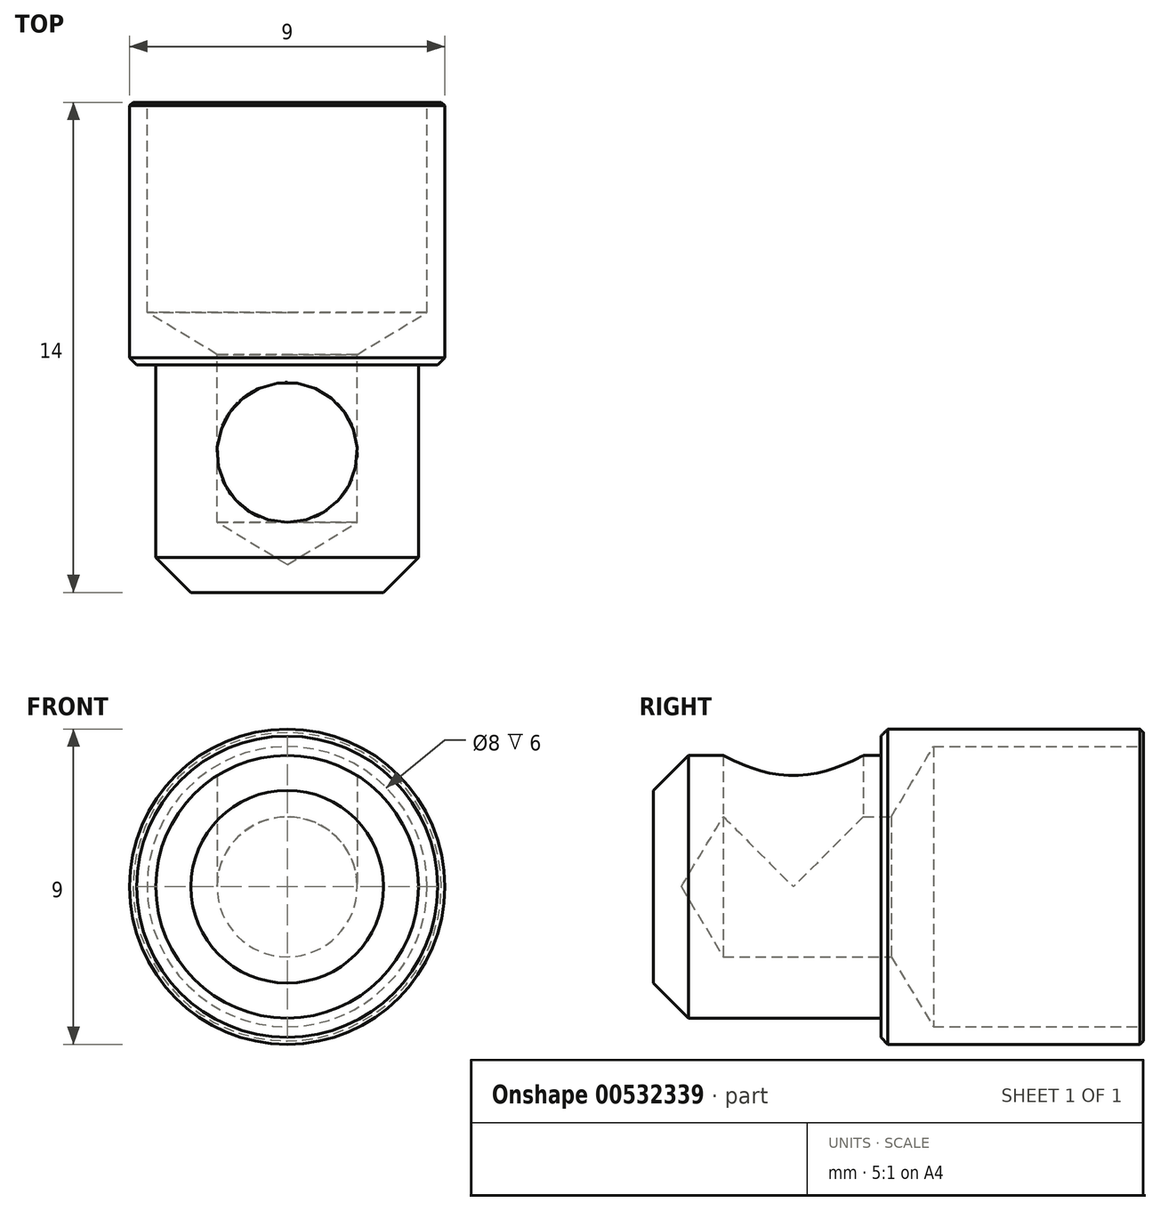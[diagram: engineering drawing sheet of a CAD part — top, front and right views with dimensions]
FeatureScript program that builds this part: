
annotation { "Feature Type Name" : "Feature", "Feature Type Description" : "" }
export const myFeature = defineFeature(function(context is Context, id is Id, definition is map)
    precondition{}
    {
        {
            var Q0;
            Q0=qCreatedBy(makeId("Front.planeOp"),FACE);
            var sketch = newSketch(context, id + "F0", { "sketchPlane" : qUnion([Q0])});
            skCircle(sketch, "E0", {"center": v(0, 0) * mm, "radius": 3.75 * mm});
            skSolve(sketch);
        }
        {
            var Q0;
            Q0 = qSketchRegion(id + "F0", true);
            extrude(context, id + "F1", {"entities" : qUnion([Q0]), "depth" : 6.5 * mm, "offsetDistance" : 25 * mm});
        }
        {
            var Q0;
            Q0=makeQuery(id+"F1.opExtrude","CAP_EDGE",EDGE,{"disambiguationData":[OSD([sQuery(id+"F0.wireOp",EDGE,"E0")])],"isStart":false});
            chamfer(context, id + "F2", {"entities" : qUnion([Q0]), "width" : 1 * mm, "tangentPropagation" : true});
        }
        {
            var Q0;
            Q0=makeQuery(id+"F1.opExtrude","CAP_FACE",FACE,{"disambiguationData":[OSD([sQuery(id+"F0.wireOp",EDGE,"E0")])],"isStart":true});
            var sketch = newSketch(context, id + "F3", { "sketchPlane" : qUnion([Q0])});
            skCircle(sketch, "E1", {"center": v(0, 0) * mm, "radius": 4.5 * mm});
            skSolve(sketch);
        }
        {
            var Q0;
            Q0 = qSketchRegion(id + "F3", true);
            extrude(context, id + "F4", {"entities" : qUnion([Q0]), "operationType" : NewBodyOperationType.ADD, "depth" : 7.5 * mm, "offsetDistance" : 25 * mm});
        }
        {
            var Q0;
            Q0=makeQuery(id+"F4.opExtrude","CAP_EDGE",EDGE,{"disambiguationData":[OSD([sQuery(id+"F3.wireOp",EDGE,"E1")])],"isStart":true});
            chamfer(context, id + "F5", {"entities" : qUnion([Q0]), "width" : 0.2 * mm, "tangentPropagation" : true});
        }
        {
            var Q0;
            Q0=makeQuery(id+"F4.opExtrude","CAP_FACE",FACE,{"disambiguationData":[OSD([sQuery(id+"F3.wireOp",EDGE,"E1")])],"isStart":false});
            var sketch = newSketch(context, id + "F6", { "sketchPlane" : qUnion([Q0])});
            skCircle(sketch, "E2", {"center": v(0, 0) * mm, "radius": 4 * mm});
            skCircle(sketch, "E3", {"center": v(0, 0) * mm, "radius": 2 * mm});
            skSolve(sketch);
        }
        {
            var Q0;
            Q0=sQuery(id+"F6.wireOp",VERTEX,"E2.center");
            var Q1;
            Q1=makeQuery(id+"F1.opExtrude","SWEPT_BODY",BODY,{"disambiguationData":[OSD([sQuery(id+"F0.wireOp",EDGE,"E0")])]});
            hole(context, id + "F7", {"style" : HoleStyle.SIMPLE, "endStyle" : HoleEndStyle.BLIND, "holeDiameter" : 4 * mm, "holeDepth" : 12 * mm, "isTappedThrough" : true, "tappedDepth" : 12 * mm, "tapClearance" : 3, "locations" : qUnion([Q0]), "scope" : qUnion([Q1])});
        }
        {
            var Q0;
            Q0=makeQuery(id+"F4.opExtrude","CAP_FACE",FACE,{"disambiguationData":[OSD([sQuery(id+"F3.wireOp",EDGE,"E1")])],"isStart":false});
            var sketch = newSketch(context, id + "F8", { "sketchPlane" : qUnion([Q0])});
            skCircle(sketch, "E4", {"center": v(0, 0) * mm, "radius": 4 * mm});
            skSolve(sketch);
        }
        {
            var Q0;
            Q0=sQuery(id+"F8.wireOp",VERTEX,"E4.center");
            var Q1;
            Q1=makeQuery(id+"F1.opExtrude","SWEPT_BODY",BODY,{"disambiguationData":[OSD([sQuery(id+"F0.wireOp",EDGE,"E0")])]});
            hole(context, id + "F9", {"style" : HoleStyle.SIMPLE, "endStyle" : HoleEndStyle.BLIND, "holeDiameter" : 8 * mm, "holeDepth" : 6 * mm, "isTappedThrough" : true, "tappedDepth" : 12 * mm, "tapClearance" : 3, "locations" : qUnion([Q0]), "scope" : qUnion([Q1])});
        }
        {
            var Q0;
            Q0=qCreatedBy(makeId("Top.planeOp"),FACE);
            var sketch = newSketch(context, id + "F10", { "sketchPlane" : qUnion([Q0])});
            skLineSegment(sketch, "E5", {"start": v(0, 8.2) * mm, "end": v(0, -6.84) * mm, "construction": true});
            skLineSegment(sketch, "E6", {"start": v(-6.1, 0) * mm, "end": v(5.62, 0) * mm, "construction": true});
            skPoint(sketch, "E7", {"position": v(0, -2.5) * mm});
            skCircle(sketch, "E8", {"center": v(0, -2.5) * mm, "radius": 2 * mm});
            skSolve(sketch);
        }
        {
            var Q0;
            Q0=sQuery(id+"F10.wireOp",VERTEX,"E7");
            var Q1;
            Q1=makeQuery(id+"F1.opExtrude","SWEPT_BODY",BODY,{"disambiguationData":[OSD([sQuery(id+"F0.wireOp",EDGE,"E0")])]});
            hole(context, id + "F11", {"style" : HoleStyle.SIMPLE, "endStyle" : HoleEndStyle.BLIND, "oppositeDirection" : true, "holeDiameter" : 4 * mm, "holeDepth" : 5 * mm, "isTappedThrough" : true, "tappedDepth" : 12 * mm, "tapClearance" : 3, "locations" : qUnion([Q0]), "scope" : qUnion([Q1])});
        }
        {
            var Q0;
            Q0=makeQuery(id+"F11.hole-0.boolean.opBoolean","INTERSECT",EDGE,{"derivedFrom":[makeQuery(id+"F1.opExtrude","SWEPT_FACE",FACE,{"disambiguationData":[OSD([sQuery(id+"F0.wireOp",EDGE,"E0")])]}),makeQuery(id+"F11.hole-0.opRevolve","SWEPT_FACE",FACE,{"disambiguationData":[OSD([sQuery(id+"F11.hole-0.sketch.wireOp",EDGE,"core_line_2")])]})]});
            var Q1;
            Q1=makeQuery(id+"F4.opExtrude","CAP_EDGE",EDGE,{"disambiguationData":[OSD([sQuery(id+"F3.wireOp",EDGE,"E1")])],"isStart":false});
            chamfer(context, id + "F12", {"entities" : qUnion([Q0, Q1]), "width" : 0.1 * mm, "tangentPropagation" : true});
        }
    });
